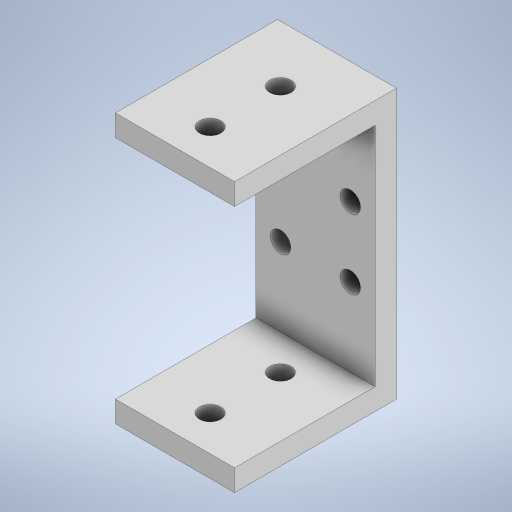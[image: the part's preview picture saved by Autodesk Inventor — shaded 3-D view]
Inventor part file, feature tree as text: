
AUTODESK INVENTOR PART (.ipt)
format: ipt  version: 2023 (Build 270158000, 158)  size: 283,136 bytes
history: native  units: mm
features: extrude x3, sketch x3
ambient origin geometry x8: Origin, YZ Plane, XZ Plane, XY Plane, X Axis, Y Axis, Z Axis, Center Point
bodies: Solid1 (feature_tree)
feature tree (6):
  extrude  "Extrusion1"  Depth=10.0mm TaperAngle=0.0deg
  extrude  "Extrusion2"  Depth=10.0mm
  extrude  "Extrusion3"  Depth=10.0mm
  sketch  "Sketch1"  dims[d2=125.5mm d3=10.0mm d4=0.0mm]
  sketch  "Sketch2"  dims[d5=10.0mm d6=10.0mm]
  sketch  "Sketch3"  dims[d7=65.5mm d8=0.0mm d9=10.0mm d10=10.0mm d11=0.0mm d12=0.0mm]
